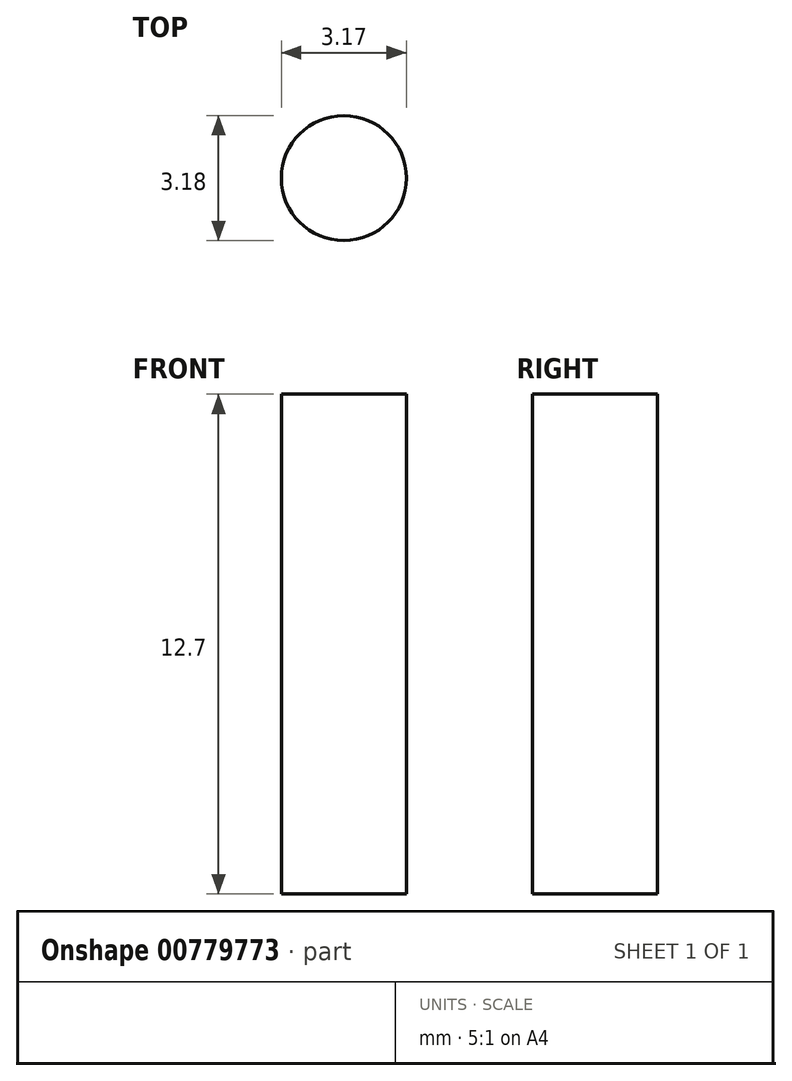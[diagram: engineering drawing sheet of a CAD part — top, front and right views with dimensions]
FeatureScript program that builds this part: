
annotation { "Feature Type Name" : "Feature", "Feature Type Description" : "" }
export const myFeature = defineFeature(function(context is Context, id is Id, definition is map)
    precondition{}
    {
        {
            var Q0;
            Q0=qCreatedBy(makeId("Top.planeOp"),FACE);
            var sketch = newSketch(context, id + "F0", { "sketchPlane" : qUnion([Q0])});
            skCircle(sketch, "E0", {"center": v(-20.78, -5.28) * mm, "radius": 1.59 * mm});
            skSolve(sketch);
        }
        {
            var Q0;
            Q0=makeQuery(id+"F0.imprint","IMPRINT",FACE,{"disambiguationData":[TD([[makeQuery(id+"F0.imprint","IMPRINT",EDGE,{"derivedFrom":sQuery(id+"F0.wireOp",EDGE,"E0")}),1.0]])]});
            extrude(context, id + "F1", {"entities" : qUnion([Q0]), "depth" : 12.7 * mm, "offsetDistance" : 25.4 * mm});
        }
    });
